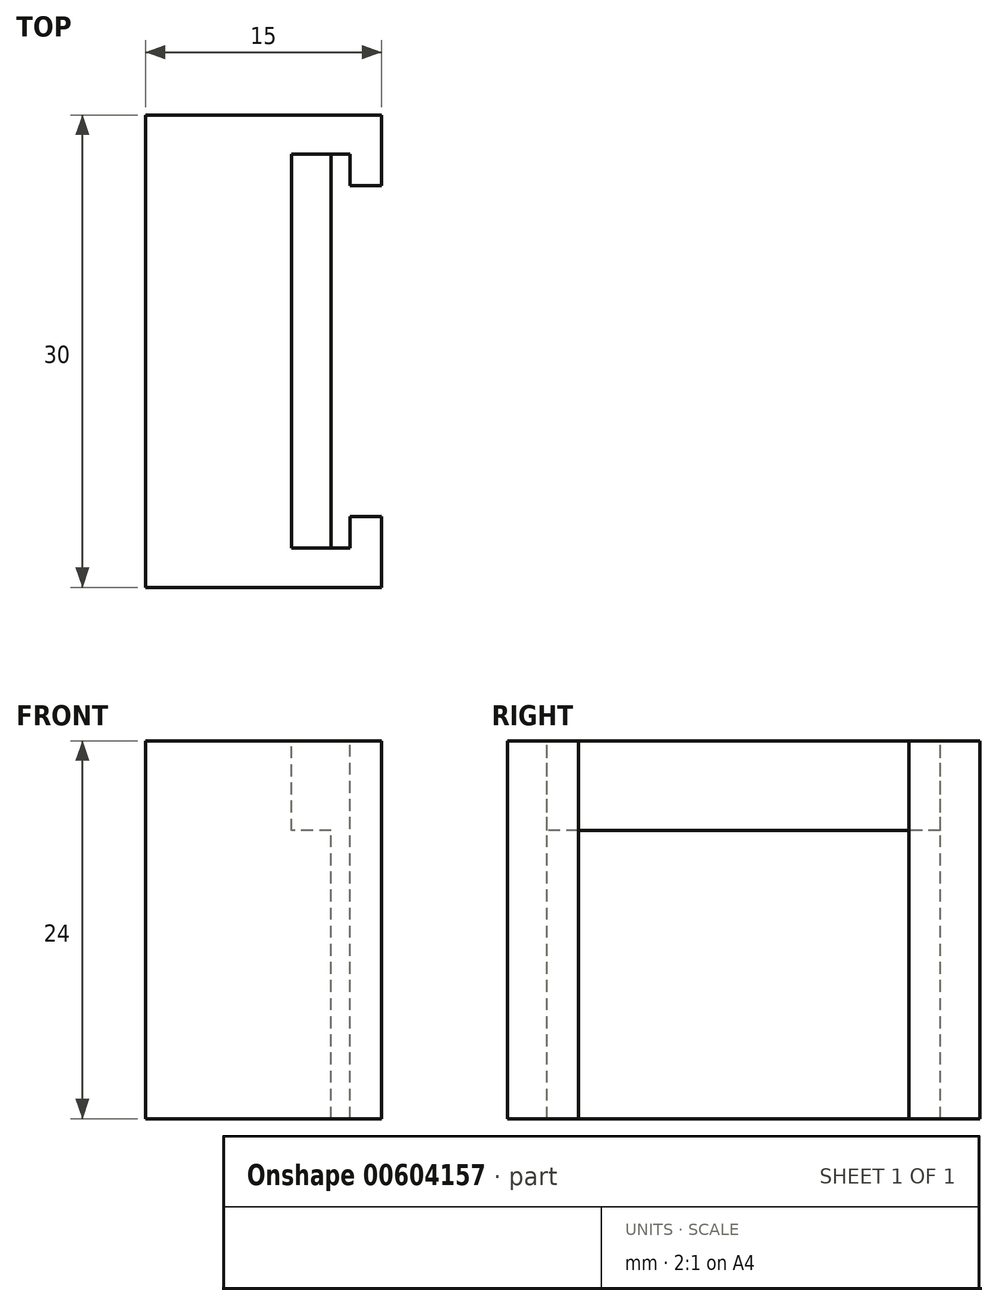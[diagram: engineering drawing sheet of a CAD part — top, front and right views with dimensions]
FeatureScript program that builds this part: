
annotation { "Feature Type Name" : "Feature", "Feature Type Description" : "" }
export const myFeature = defineFeature(function(context is Context, id is Id, definition is map)
    precondition{}
    {
        {
            var Q0;
            Q0=qCreatedBy(makeId("Front.planeOp"),FACE);
            var sketch = newSketch(context, id + "F0", { "sketchPlane" : qUnion([Q0])});
            skLineSegment(sketch, "E0.bottom", {"start": v(0, 0) * mm, "end": v(15, 0) * mm});
            skLineSegment(sketch, "E0.top", {"start": v(0, 24) * mm, "end": v(15, 24) * mm});
            skLineSegment(sketch, "E0.left", {"start": v(0, 0) * mm, "end": v(0, 24) * mm});
            skLineSegment(sketch, "E0.right", {"start": v(15, 0) * mm, "end": v(15, 24) * mm});
            skSolve(sketch);
        }
        {
            var Q0;
            Q0 = qSketchRegion(id + "F0", true);
            extrude(context, id + "F1", {"entities" : qUnion([Q0]), "depth" : 30 * mm, "offsetDistance" : 25 * mm});
        }
        {
            var Q0;
            Q0=makeQuery(id+"F1.opExtrude","SWEPT_FACE",FACE,{"disambiguationData":[OSD([sQuery(id+"F0.wireOp",EDGE,"E0.top")])]});
            var sketch = newSketch(context, id + "F2", { "sketchPlane" : qUnion([Q0])});
            skLineSegment(sketch, "E1.bottom", {"start": v(11.8, -2.5) * mm, "end": v(13, -2.5) * mm});
            skLineSegment(sketch, "E1.top", {"start": v(11.8, -27.5) * mm, "end": v(13, -27.5) * mm});
            skLineSegment(sketch, "E1.left", {"start": v(11.8, -2.5) * mm, "end": v(11.8, -27.5) * mm});
            skLineSegment(sketch, "E1.right", {"start": v(13, -2.5) * mm, "end": v(13, -27.5) * mm});
            skSolve(sketch);
        }
        {
            var Q0;
            Q0 = qSketchRegion(id + "F2", true);
            extrude(context, id + "F3", {"entities" : qUnion([Q0]), "operationType" : NewBodyOperationType.REMOVE, "endBound" : BoundingType.THROUGH_ALL, "oppositeDirection" : true, "depth" : 25 * mm, "offsetDistance" : 25 * mm});
        }
        {
            var Q0;
            Q0=makeQuery(id+"F1.opExtrude","SWEPT_FACE",FACE,{"disambiguationData":[OSD([sQuery(id+"F0.wireOp",EDGE,"E0.top")])]});
            var sketch = newSketch(context, id + "F4", { "sketchPlane" : qUnion([Q0])});
            skLineSegment(sketch, "E2.bottom", {"start": v(13, -4.5) * mm, "end": v(15, -4.5) * mm});
            skLineSegment(sketch, "E2.top", {"start": v(13, -25.5) * mm, "end": v(15, -25.5) * mm});
            skLineSegment(sketch, "E2.left", {"start": v(13, -4.5) * mm, "end": v(13, -25.5) * mm});
            skLineSegment(sketch, "E2.right", {"start": v(15, -4.5) * mm, "end": v(15, -25.5) * mm});
            skSolve(sketch);
        }
        {
            var Q0;
            Q0 = qSketchRegion(id + "F4", true);
            extrude(context, id + "F5", {"entities" : qUnion([Q0]), "operationType" : NewBodyOperationType.REMOVE, "endBound" : BoundingType.THROUGH_ALL, "oppositeDirection" : true, "depth" : 25 * mm, "offsetDistance" : 25 * mm});
        }
        {
            var Q0;
            Q0=makeQuery(id+"F1.opExtrude","SWEPT_FACE",FACE,{"disambiguationData":[OSD([sQuery(id+"F0.wireOp",EDGE,"E0.top")])]});
            var sketch = newSketch(context, id + "F6", { "sketchPlane" : qUnion([Q0])});
            skLineSegment(sketch, "E3.bottom", {"start": v(11.8, -2.5) * mm, "end": v(9.3, -2.5) * mm});
            skLineSegment(sketch, "E3.top", {"start": v(11.8, -27.5) * mm, "end": v(9.3, -27.5) * mm});
            skLineSegment(sketch, "E3.left", {"start": v(11.8, -2.5) * mm, "end": v(11.8, -27.5) * mm});
            skLineSegment(sketch, "E3.right", {"start": v(9.3, -2.5) * mm, "end": v(9.3, -27.5) * mm});
            skSolve(sketch);
        }
        {
            var Q0;
            Q0 = qSketchRegion(id + "F6", true);
            extrude(context, id + "F7", {"entities" : qUnion([Q0]), "operationType" : NewBodyOperationType.REMOVE, "oppositeDirection" : true, "depth" : 5.7 * mm, "offsetDistance" : 25 * mm});
        }
    });
